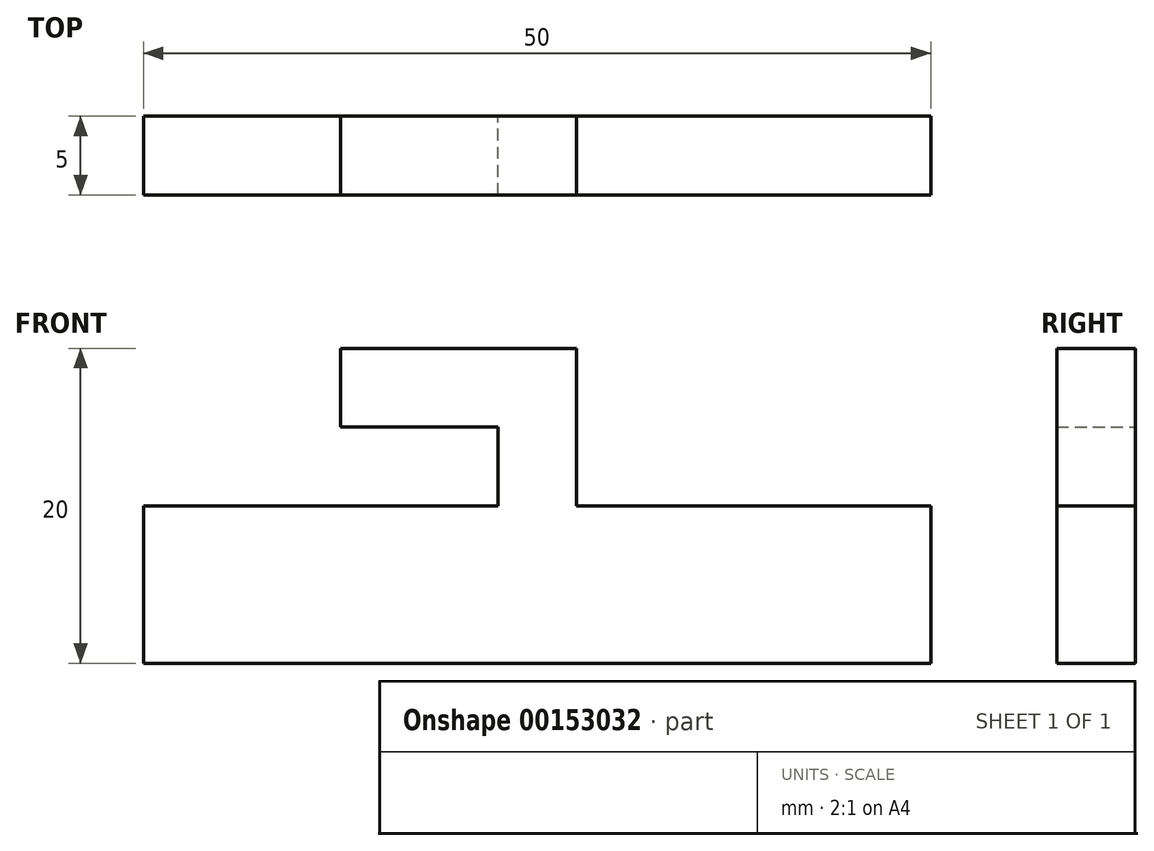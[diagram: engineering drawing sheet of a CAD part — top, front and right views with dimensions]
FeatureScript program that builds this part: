
annotation { "Feature Type Name" : "Feature", "Feature Type Description" : "" }
export const myFeature = defineFeature(function(context is Context, id is Id, definition is map)
    precondition{}
    {
        {
            var Q0;
            Q0=qCreatedBy(makeId("Front.planeOp"),FACE);
            var sketch = newSketch(context, id + "F0", { "sketchPlane" : qUnion([Q0])});
            skLineSegment(sketch, "E0.bottom", {"start": v(25, -5) * mm, "end": v(-25, -5) * mm});
            skLineSegment(sketch, "E0.top", {"start": v(25, 5) * mm, "end": v(-25, 5) * mm});
            skLineSegment(sketch, "E0.left", {"start": v(25, -5) * mm, "end": v(25, 5) * mm});
            skLineSegment(sketch, "E0.right", {"start": v(-25, -5) * mm, "end": v(-25, 5) * mm});
            skPoint(sketch, "E0.middle", {"position": v(0, 0) * mm});
            skLineSegment(sketch, "E1", {"start": v(-2.5, 5) * mm, "end": v(-2.5, 10) * mm});
            skLineSegment(sketch, "E2", {"start": v(-2.5, 10) * mm, "end": v(-12.5, 10) * mm});
            skLineSegment(sketch, "E3", {"start": v(-12.5, 10) * mm, "end": v(-12.5, 15) * mm});
            skLineSegment(sketch, "E4", {"start": v(-12.5, 15) * mm, "end": v(2.5, 15) * mm});
            skLineSegment(sketch, "E5", {"start": v(2.5, 15) * mm, "end": v(2.5, 5) * mm});
            skSolve(sketch);
        }
        {
            var Q0;
            Q0=makeQuery(id+"F0.imprint","IMPRINT",FACE,{"disambiguationData":[TD([[makeQuery(id+"F0.imprint","IMPRINT",EDGE,{"derivedFrom":sQuery(id+"F0.wireOp",EDGE,"E0.bottom")}),-1.0]])]});
            var Q1;
            {var subQ0=sQuery(id+"F0.wireOp",EDGE,"E1");Q1=makeQuery(id+"F0.imprint","IMPRINT",FACE,{"disambiguationData":[TD([[makeQuery(id+"F0.imprint","IMPRINT",EDGE,{"derivedFrom":subQ0}),-1.0]])]});}
            extrude(context, id + "F1", {"entities" : qUnion([Q0, Q1]), "depth" : 5 * mm});
        }
    });
